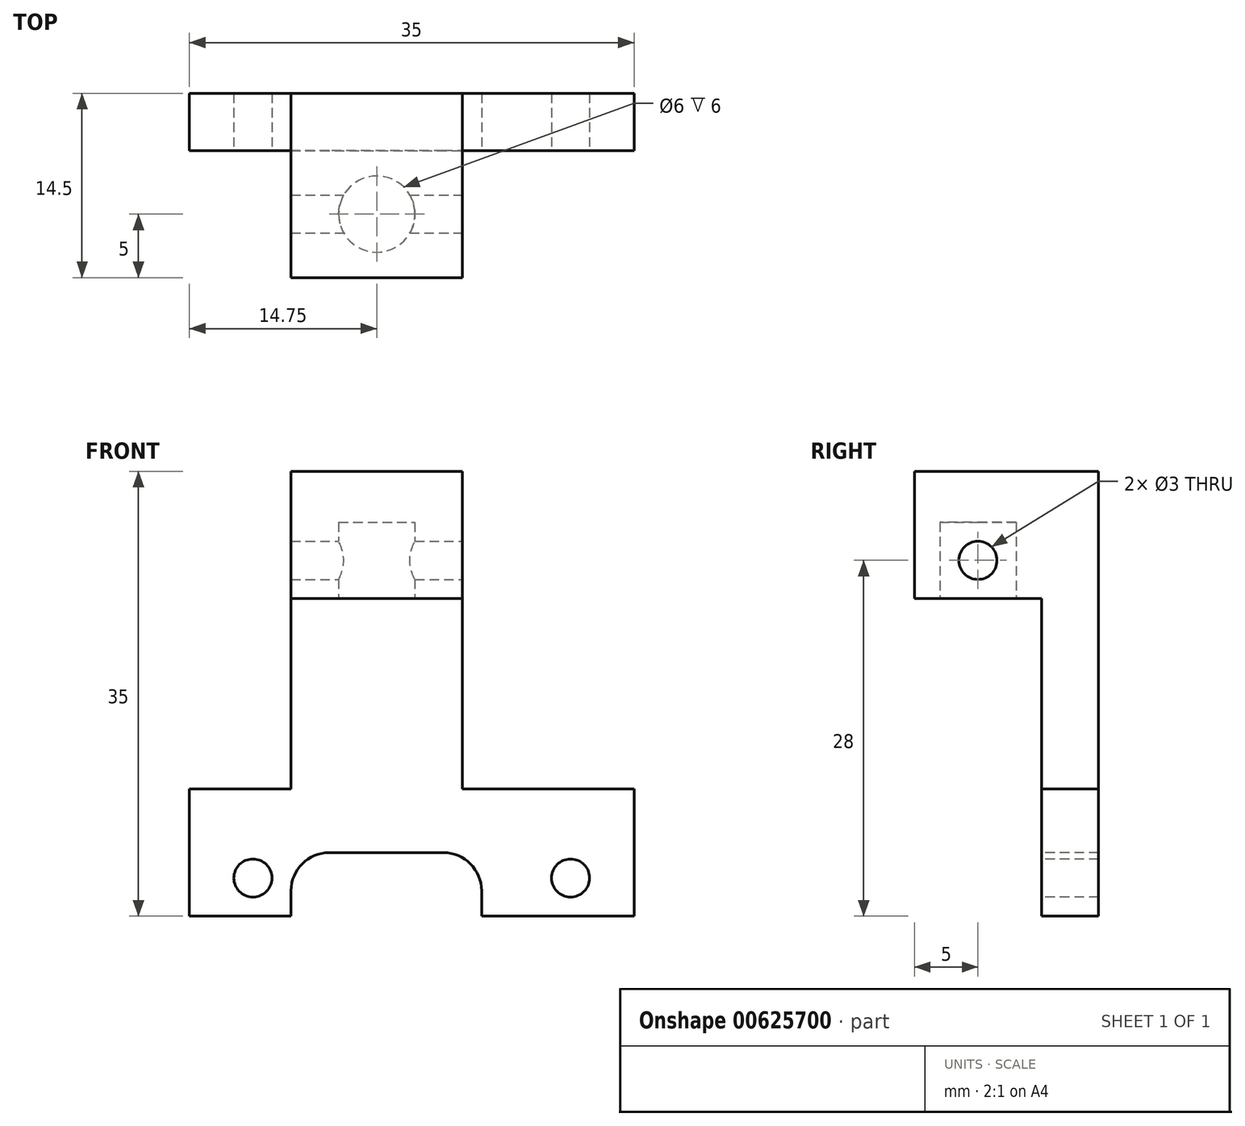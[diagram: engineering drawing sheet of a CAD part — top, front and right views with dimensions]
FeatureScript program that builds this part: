
annotation { "Feature Type Name" : "Feature", "Feature Type Description" : "" }
export const myFeature = defineFeature(function(context is Context, id is Id, definition is map)
    precondition{}
    {
        {
            var Q0;
            Q0=qCreatedBy(makeId("Front.planeOp"),FACE);
            var sketch = newSketch(context, id + "F0", { "sketchPlane" : qUnion([Q0])});
            skLineSegment(sketch, "E0.bottom", {"start": v(-17.5, 17) * mm, "end": v(17.5, 17) * mm});
            skLineSegment(sketch, "E0.top", {"start": v(-17.5, -20) * mm, "end": v(17.5, -20) * mm});
            skLineSegment(sketch, "E0.left", {"start": v(-17.5, 17) * mm, "end": v(-17.5, -20) * mm});
            skLineSegment(sketch, "E0.right", {"start": v(17.5, 17) * mm, "end": v(17.5, -20) * mm});
            skPoint(sketch, "E0.middle", {"position": v(0, -1.5) * mm});
            skSolve(sketch);
        }
        {
            var Q0;
            Q0=makeQuery(id+"F0.imprint","IMPRINT",FACE,{"disambiguationData":[TD([[makeQuery(id+"F0.imprint","IMPRINT",EDGE,{"derivedFrom":sQuery(id+"F0.wireOp",EDGE,"E0.bottom")}),-1.0]])]});
            extrude(context, id + "F1", {"entities" : qUnion([Q0]), "depth" : 4.5 * mm, "offsetDistance" : 25 * mm});
        }
        {
            var Q0;
            Q0=makeQuery(id+"F1.opExtrude","CAP_FACE",FACE,{"disambiguationData":[OSD([sQuery(id+"F0.wireOp",EDGE,"E0.bottom"),sQuery(id+"F0.wireOp",EDGE,"E0.top"),sQuery(id+"F0.wireOp",EDGE,"E0.left"),sQuery(id+"F0.wireOp",EDGE,"E0.right")])],"isStart":false});
            var sketch = newSketch(context, id + "F2", { "sketchPlane" : qUnion([Q0])});
            skCircle(sketch, "E1", {"center": v(12.5, -15) * mm, "radius": 1.5 * mm});
            skCircle(sketch, "E2.MirrorC", {"center": v(-12.5, -15) * mm, "radius": 1.5 * mm});
            skSolve(sketch);
        }
        {
            var Q0;
            Q0=qSketchRegion(id+"F2",true);
            extrude(context, id + "F3", {"entities" : qUnion([Q0]), "operationType" : NewBodyOperationType.REMOVE, "oppositeDirection" : true, "depth" : 10 * mm, "offsetDistance" : 25 * mm});
        }
        {
            var Q0;
            Q0=makeQuery(id+"F1.opExtrude","CAP_FACE",FACE,{"disambiguationData":[OSD([sQuery(id+"F0.wireOp",EDGE,"E0.bottom"),sQuery(id+"F0.wireOp",EDGE,"E0.top"),sQuery(id+"F0.wireOp",EDGE,"E0.left"),sQuery(id+"F0.wireOp",EDGE,"E0.right")])],"isStart":false});
            var sketch = newSketch(context, id + "F4", { "sketchPlane" : qUnion([Q0])});
            skLineSegment(sketch, "E3.bottom", {"start": v(-17.5, 17) * mm, "end": v(17.5, 17) * mm});
            skLineSegment(sketch, "E3.top", {"start": v(-17.5, 7) * mm, "end": v(17.5, 7) * mm});
            skLineSegment(sketch, "E3.left", {"start": v(-17.5, 17) * mm, "end": v(-17.5, 7) * mm});
            skLineSegment(sketch, "E3.right", {"start": v(17.5, 17) * mm, "end": v(17.5, 7) * mm});
            skSolve(sketch);
        }
        {
            var Q0;
            Q0=qSketchRegion(id+"F4",true);
            extrude(context, id + "F5", {"entities" : qUnion([Q0]), "operationType" : NewBodyOperationType.ADD, "depth" : 10 * mm, "offsetDistance" : 25 * mm});
        }
        {
            var Q0;
            Q0=makeQuery(id+"F5.opExtrude","SWEPT_FACE",FACE,{"disambiguationData":[OSD([sQuery(id+"F4.wireOp",EDGE,"E3.top")])]});
            var sketch = newSketch(context, id + "F6", { "sketchPlane" : qUnion([Q0])});
            skCircle(sketch, "E4", {"center": v(-2.75, 9.5) * mm, "radius": 3 * mm});
            skPoint(sketch, "E4.centerSnap0", {"position": v(14.75, 9.5) * mm});
            skPoint(sketch, "E4.centerSnap1", {"position": v(-2.75, 14.5) * mm});
            skSolve(sketch);
        }
        {
            var Q0;
            Q0=qSketchRegion(id+"F6",true);
            extrude(context, id + "F7", {"entities" : qUnion([Q0]), "operationType" : NewBodyOperationType.REMOVE, "oppositeDirection" : true, "depth" : 6 * mm, "offsetDistance" : 25 * mm});
        }
        {
            var Q0;
            Q0=makeQuery(id+"F1.opExtrude","SWEPT_FACE",FACE,{"disambiguationData":[OSD([sQuery(id+"F0.wireOp",EDGE,"E0.top")])]});
            var sketch = newSketch(context, id + "F8", { "sketchPlane" : qUnion([Q0])});
            skLineSegment(sketch, "E5.0.0", {"start": v(-17.5, 0) * mm, "end": v(17.5, 0) * mm});
            skLineSegment(sketch, "E5.0.1", {"start": v(17.5, 0) * mm, "end": v(17.5, 4.5) * mm});
            skLineSegment(sketch, "E5.0.2", {"start": v(17.5, 4.5) * mm, "end": v(-17.5, 4.5) * mm});
            skLineSegment(sketch, "E5.0.3", {"start": v(-17.5, 4.5) * mm, "end": v(-17.5, 0) * mm});
            skSolve(sketch);
        }
        {
            var Q0;
            Q0=qSketchRegion(id+"F8",true);
            extrude(context, id + "F9", {"entities" : qUnion([Q0]), "operationType" : NewBodyOperationType.REMOVE, "oppositeDirection" : true, "depth" : 2 * mm, "offsetDistance" : 25 * mm});
        }
        {
            var Q0;
            Q0=makeQuery(id+"F5.opExtrude","CAP_FACE",FACE,{"disambiguationData":[OSD([sQuery(id+"F4.wireOp",EDGE,"E3.bottom"),sQuery(id+"F4.wireOp",EDGE,"E3.top"),sQuery(id+"F4.wireOp",EDGE,"E3.left"),sQuery(id+"F4.wireOp",EDGE,"E3.right")])],"isStart":false});
            var sketch = newSketch(context, id + "F10", { "sketchPlane" : qUnion([Q0])});
            skLineSegment(sketch, "E6.bottom", {"start": v(-17.5, 17) * mm, "end": v(-9.5, 17) * mm});
            skLineSegment(sketch, "E6.top", {"start": v(-17.5, -8) * mm, "end": v(-9.5, -8) * mm});
            skLineSegment(sketch, "E6.left", {"start": v(-17.5, 17) * mm, "end": v(-17.5, -8) * mm});
            skLineSegment(sketch, "E6.right", {"start": v(-9.5, 17) * mm, "end": v(-9.5, -8) * mm});
            skLineSegment(sketch, "E7.bottom", {"start": v(17.5, 17) * mm, "end": v(4, 17) * mm});
            skLineSegment(sketch, "E7.top", {"start": v(17.5, -8) * mm, "end": v(4, -8) * mm});
            skLineSegment(sketch, "E7.left", {"start": v(17.5, 17) * mm, "end": v(17.5, -8) * mm});
            skLineSegment(sketch, "E7.right", {"start": v(4, 17) * mm, "end": v(4, -8) * mm});
            skSolve(sketch);
        }
        {
            var Q0;
            Q0=qSketchRegion(id+"F10",true);
            extrude(context, id + "F11", {"entities" : qUnion([Q0]), "operationType" : NewBodyOperationType.REMOVE, "endBound" : BoundingType.THROUGH_ALL, "oppositeDirection" : true, "depth" : 25 * mm, "offsetDistance" : 25 * mm});
        }
        {
            var Q0;
            Q0=makeQuery(id+"F1.opExtrude","CAP_FACE",FACE,{"disambiguationData":[OSD([sQuery(id+"F0.wireOp",EDGE,"E0.bottom"),sQuery(id+"F0.wireOp",EDGE,"E0.top"),sQuery(id+"F0.wireOp",EDGE,"E0.left"),sQuery(id+"F0.wireOp",EDGE,"E0.right")])],"isStart":false});
            var sketch = newSketch(context, id + "F12", { "sketchPlane" : qUnion([Q0])});
            skLineSegment(sketch, "E8.bottom", {"start": v(5.5, -18) * mm, "end": v(-9.5, -18) * mm});
            skLineSegment(sketch, "E8.top", {"start": v(5.5, -13) * mm, "end": v(-9.5, -13) * mm});
            skLineSegment(sketch, "E8.left", {"start": v(5.5, -18) * mm, "end": v(5.5, -13) * mm});
            skLineSegment(sketch, "E8.right", {"start": v(-9.5, -18) * mm, "end": v(-9.5, -13) * mm});
            skSolve(sketch);
        }
        {
            var Q0;
            Q0 = qSketchRegion(id + "F12", true);
            extrude(context, id + "F13", {"entities" : qUnion([Q0]), "operationType" : NewBodyOperationType.REMOVE, "endBound" : BoundingType.THROUGH_ALL, "oppositeDirection" : true, "depth" : 25 * mm, "offsetDistance" : 25 * mm});
        }
        {
            var Q0;
            Q0=makeQuery(id+"F13.boolean.opBoolean","COPY",EDGE,{"derivedFrom":makeQuery(id+"F13.opExtrude","SWEPT_EDGE",EDGE,{"disambiguationData":[OSD([sQuery(id+"F12.wireOp",EDGE,"E8.top"),sQuery(id+"F12.wireOp",EDGE,"E8.left")])]})});
            var Q1;
            Q1=makeQuery(id+"F13.boolean.opBoolean","COPY",EDGE,{"derivedFrom":makeQuery(id+"F13.opExtrude","SWEPT_EDGE",EDGE,{"disambiguationData":[OSD([sQuery(id+"F12.wireOp",EDGE,"E8.top"),sQuery(id+"F12.wireOp",EDGE,"E8.right")])]})});
            fillet(context, id + "F14", {"entities" : qUnion([Q0, Q1]), "radius" : 3 * mm, "tangentPropagation" : true, "allowEdgeOverflow" : false});
        }
        {
            var Q0;
            Q0=makeQuery(id+"F11.boolean.opBoolean","COPY",FACE,{"derivedFrom":makeQuery(id+"F11.opExtrude","SWEPT_FACE",FACE,{"disambiguationData":[OSD([sQuery(id+"F10.wireOp",EDGE,"E7.right")])]})});
            var sketch = newSketch(context, id + "F15", { "sketchPlane" : qUnion([Q0])});
            skCircle(sketch, "E9", {"center": v(-9.5, 10) * mm, "radius": 1.5 * mm});
            skSolve(sketch);
        }
        {
            var Q0;
            Q0 = qSketchRegion(id + "F15", true);
            extrude(context, id + "F16", {"entities" : qUnion([Q0]), "operationType" : NewBodyOperationType.REMOVE, "endBound" : BoundingType.THROUGH_ALL, "oppositeDirection" : true, "depth" : 25 * mm, "offsetDistance" : 25 * mm});
        }
    });
